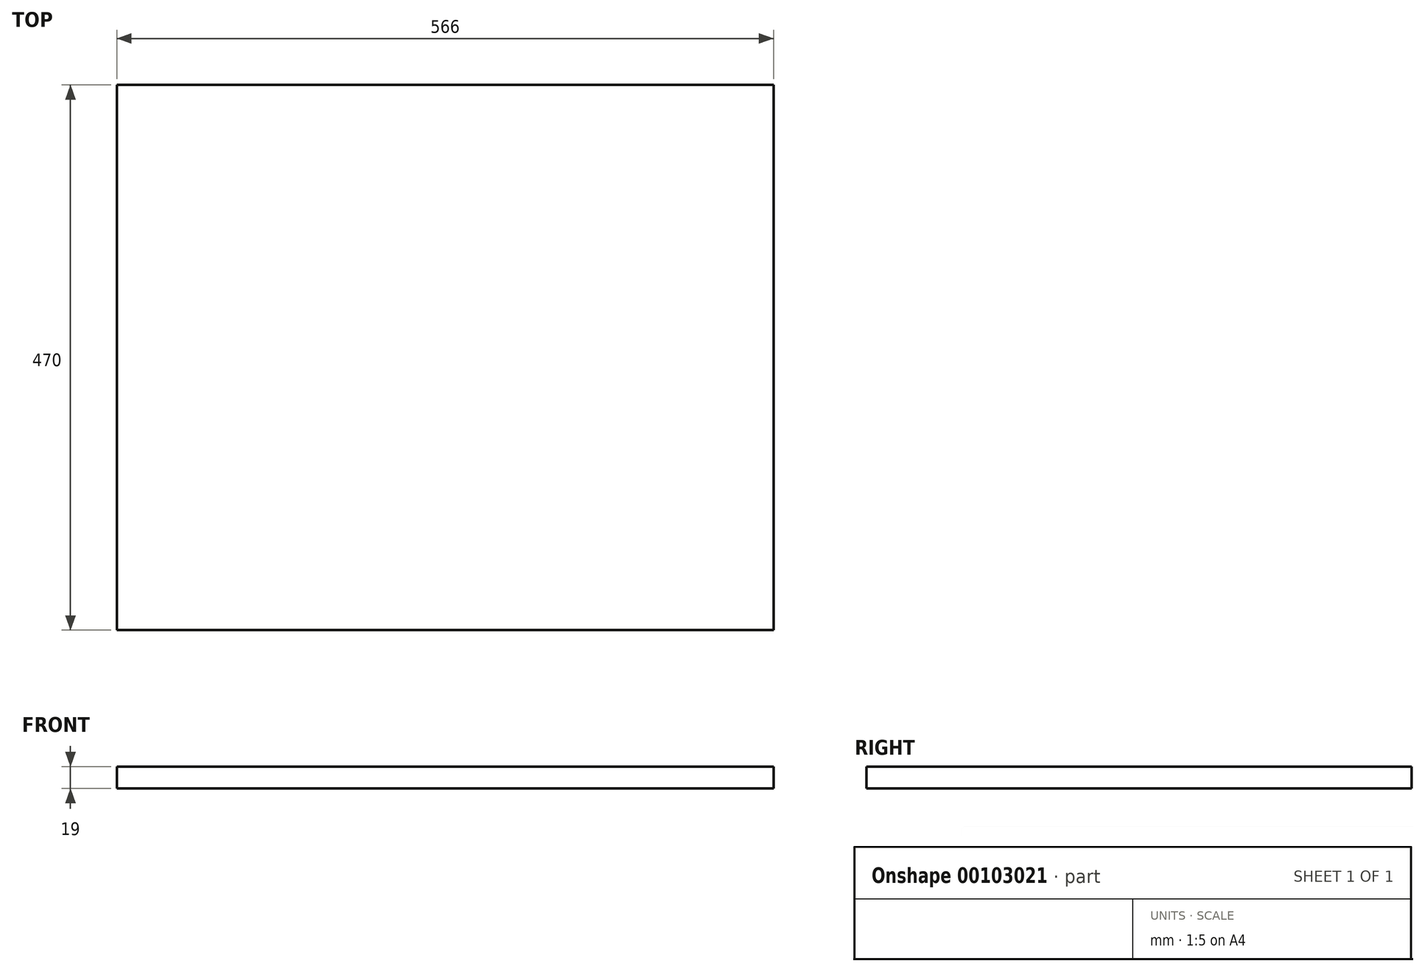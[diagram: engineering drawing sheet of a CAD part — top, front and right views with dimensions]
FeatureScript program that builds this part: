
annotation { "Feature Type Name" : "Feature", "Feature Type Description" : "" }
export const myFeature = defineFeature(function(context is Context, id is Id, definition is map)
    precondition{}
    {
        {
            var Q0;
            Q0=qCreatedBy(makeId("Top.planeOp"),FACE);
            var sketch = newSketch(context, id + "F0", { "sketchPlane" : qUnion([Q0])});
            skLineSegment(sketch, "E0.bottom", {"start": v(-70.96, 65.05) * mm, "end": v(495.04, 65.05) * mm});
            skLineSegment(sketch, "E0.top", {"start": v(-70.96, -404.95) * mm, "end": v(495.04, -404.95) * mm});
            skLineSegment(sketch, "E0.left", {"start": v(-70.96, 65.05) * mm, "end": v(-70.96, -404.95) * mm});
            skLineSegment(sketch, "E0.right", {"start": v(495.04, 65.05) * mm, "end": v(495.04, -404.95) * mm});
            skSolve(sketch);
        }
        {
            var Q0;
            Q0=qSketchRegion(id+"F0",true);
            extrude(context, id + "F1", {"entities" : qUnion([Q0]), "depth" : 19 * mm});
        }
    });
